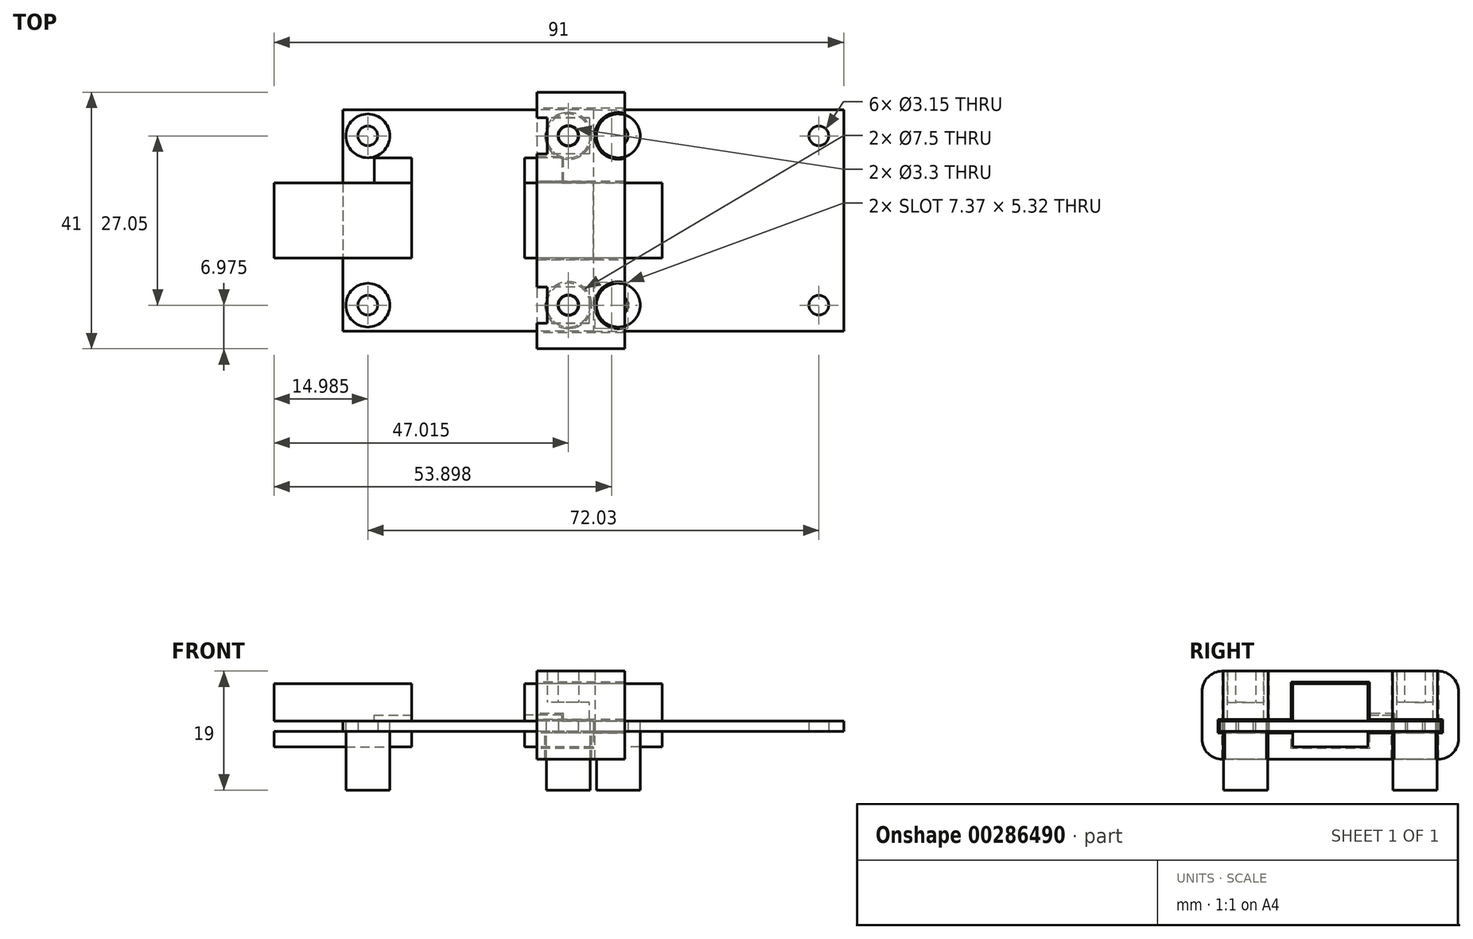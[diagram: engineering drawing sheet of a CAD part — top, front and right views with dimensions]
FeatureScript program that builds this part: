
annotation { "Feature Type Name" : "Feature", "Feature Type Description" : "" }
export const myFeature = defineFeature(function(context is Context, id is Id, definition is map)
    precondition{}
    {
        {
            var Q0;
            Q0=qCreatedBy(makeId("Top.planeOp"),FACE);
            var sketch = newSketch(context, id + "F0", { "sketchPlane" : qUnion([Q0])});
            skLineSegment(sketch, "E0.bottom", {"start": v(20, 17.7) * mm, "end": v(-20, 17.7) * mm});
            skLineSegment(sketch, "E0.top", {"start": v(20, -17.7) * mm, "end": v(-20, -17.7) * mm});
            skLineSegment(sketch, "E0.left", {"start": v(20, 17.7) * mm, "end": v(20, -17.7) * mm});
            skLineSegment(sketch, "E0.right", {"start": v(-20, 17.7) * mm, "end": v(-20, -17.7) * mm});
            skPoint(sketch, "E0.middle", {"position": v(0, 0) * mm});
            skCircle(sketch, "E1", {"center": v(-16.02, 13.52) * mm, "radius": 1.57 * mm});
            skCircle(sketch, "E2.MirrorC", {"center": v(16.02, 13.52) * mm, "radius": 1.57 * mm});
            skCircle(sketch, "E3.MirrorC", {"center": v(-16.02, -13.52) * mm, "radius": 1.57 * mm});
            skCircle(sketch, "E4.MirrorC", {"center": v(16.02, -13.52) * mm, "radius": 1.57 * mm});
            skSolve(sketch);
        }
        {
            var Q0;
            Q0 = qSketchRegion(id + "F0", true);
            extrude(context, id + "F1", {"entities" : qUnion([Q0]), "depth" : 1.6 * mm, "offsetDistance" : 25 * mm, "symmetric" : true});
        }
        {
            var Q0;
            Q0=makeQuery(id+"F1.opExtrude","CAP_FACE",FACE,{"disambiguationData":[OSD([sQuery(id+"F0.wireOp",EDGE,"E0.bottom"),sQuery(id+"F0.wireOp",EDGE,"E0.top"),sQuery(id+"F0.wireOp",EDGE,"E0.left"),sQuery(id+"F0.wireOp",EDGE,"E0.right"),sQuery(id+"F0.wireOp",EDGE,"E1"),sQuery(id+"F0.wireOp",EDGE,"E2.MirrorC"),sQuery(id+"F0.wireOp",EDGE,"E3.MirrorC"),sQuery(id+"F0.wireOp",EDGE,"E4.MirrorC")])],"isStart":false});
            var sketch = newSketch(context, id + "F2", { "sketchPlane" : qUnion([Q0])});
            skCircle(sketch, "E5", {"center": v(-16.02, 13.52) * mm, "radius": 3.5 * mm});
            skCircle(sketch, "E6", {"center": v(16.02, 13.52) * mm, "radius": 3.5 * mm});
            skCircle(sketch, "E7", {"center": v(16.02, -13.52) * mm, "radius": 3.5 * mm});
            skCircle(sketch, "E8", {"center": v(-16.02, -13.52) * mm, "radius": 3.5 * mm});
            skSolve(sketch);
        }
        {
            var Q0;
            Q0 = qSketchRegion(id + "F2", true);
            extrude(context, id + "F3", {"entities" : qUnion([Q0]), "oppositeDirection" : true, "depth" : 11 * mm, "offsetDistance" : 25 * mm});
        }
        {
            var Q0;
            Q0=makeQuery(id+"F1.opExtrude","SWEPT_FACE",FACE,{"disambiguationData":[OSD([sQuery(id+"F0.wireOp",EDGE,"E0.left")])]});
            var sketch = newSketch(context, id + "F4", { "sketchPlane" : qUnion([Q0])});
            skLineSegment(sketch, "E9.top", {"start": v(-6, -0.8) * mm, "end": v(6, -0.8) * mm});
            skLineSegment(sketch, "E10.MirrorCS", {"start": v(-6, 0.8) * mm, "end": v(6, 0.8) * mm});
            skLineSegment(sketch, "E11.bottom", {"start": v(6, 0.8) * mm, "end": v(10, 0.8) * mm});
            skLineSegment(sketch, "E11.top", {"start": v(6, 1.8) * mm, "end": v(10, 1.8) * mm});
            skLineSegment(sketch, "E11.left", {"start": v(6, 0.8) * mm, "end": v(6, 1.8) * mm});
            skLineSegment(sketch, "E11.right", {"start": v(10, 0.8) * mm, "end": v(10, 1.8) * mm});
            skLineSegment(sketch, "E12", {"start": v(-6, 0.8) * mm, "end": v(-6, 6.8) * mm});
            skLineSegment(sketch, "E13", {"start": v(-6, 6.8) * mm, "end": v(6, 6.8) * mm});
            skLineSegment(sketch, "E14", {"start": v(6, 6.8) * mm, "end": v(6, 0.8) * mm});
            skLineSegment(sketch, "E15", {"start": v(-6, -0.8) * mm, "end": v(-6, -3.3) * mm});
            skLineSegment(sketch, "E16", {"start": v(-6, -3.3) * mm, "end": v(6, -3.3) * mm});
            skLineSegment(sketch, "E17", {"start": v(6, -3.3) * mm, "end": v(6, -0.8) * mm});
            skSolve(sketch);
        }
        {
            var Q0;
            Q0 = qSketchRegion(id + "F4", true);
            extrude(context, id + "F5", {"entities" : qUnion([Q0]), "depth" : 22 * mm, "offsetDistance" : 25 * mm, "symmetric" : true});
        }
        {
            var Q0;
            Q0=makeQuery(id+"F5.opExtrude","CAP_FACE",FACE,{"disambiguationData":[OSD([sQuery(id+"F4.wireOp",EDGE,"E10.MirrorCS"),sQuery(id+"F4.wireOp",EDGE,"E11.bottom"),sQuery(id+"F4.wireOp",EDGE,"E11.top"),sQuery(id+"F4.wireOp",EDGE,"E11.right"),sQuery(id+"F4.wireOp",EDGE,"E12"),sQuery(id+"F4.wireOp",EDGE,"E13"),sQuery(id+"F4.wireOp",EDGE,"E14")])],"isStart":false});
            var sketch = newSketch(context, id + "F6", { "sketchPlane" : qUnion([Q0])});
            skLineSegment(sketch, "E18.bottom", {"start": v(6, 1.8) * mm, "end": v(10, 1.8) * mm});
            skLineSegment(sketch, "E18.top", {"start": v(6, 0.8) * mm, "end": v(10, 0.8) * mm});
            skLineSegment(sketch, "E18.left", {"start": v(6, 1.8) * mm, "end": v(6, 0.8) * mm});
            skLineSegment(sketch, "E18.right", {"start": v(10, 1.8) * mm, "end": v(10, 0.8) * mm});
            skSolve(sketch);
        }
        {
            var Q0;
            Q0 = qSketchRegion(id + "F6", true);
            extrude(context, id + "F7", {"entities" : qUnion([Q0]), "operationType" : NewBodyOperationType.REMOVE, "oppositeDirection" : true, "depth" : 16 * mm, "offsetDistance" : 25 * mm});
        }
        {
            var Q0;
            Q0=makeQuery(id+"F5.opExtrude","SWEPT_BODY",BODY,{"disambiguationData":[OSD([sQuery(id+"F4.wireOp",EDGE,"E9.bottom"),sQuery(id+"F4.wireOp",EDGE,"E9.top"),sQuery(id+"F4.wireOp",EDGE,"E9.left"),sQuery(id+"F4.wireOp",EDGE,"E9.right")])]});
            var Q1;
            Q1=makeQuery(id+"F5.opExtrude","SWEPT_BODY",BODY,{"disambiguationData":[OSD([sQuery(id+"F4.wireOp",EDGE,"d8b67e58-9760-4f35-8aba-aea9f4cf0cb30.MirrorCS"),sQuery(id+"F4.wireOp",EDGE,"fc04d03d-4783-4ae8-9673-6a9668c51ce80.MirrorCS"),sQuery(id+"F4.wireOp",EDGE,"E10.MirrorCS"),sQuery(id+"F4.wireOp",EDGE,"51854301-50fa-4171-bd93-f3eeceddffb40.MirrorCS")])]});
            var Q2;
            Q2=qCreatedBy(makeId("Right.planeOp"),FACE);
            mirror(context, id + "F8", {"entities" : qUnion([Q0, Q1]), "mirrorPlane" : qUnion([Q2])});
        }
        {
            var Q0;
            Q0=makeQuery(id+"F1.opExtrude","SWEPT_BODY",BODY,{"disambiguationData":[OSD([sQuery(id+"F0.wireOp",EDGE,"E0.bottom"),sQuery(id+"F0.wireOp",EDGE,"E0.top"),sQuery(id+"F0.wireOp",EDGE,"E0.left"),sQuery(id+"F0.wireOp",EDGE,"E0.right"),sQuery(id+"F0.wireOp",EDGE,"E1"),sQuery(id+"F0.wireOp",EDGE,"E2.MirrorC"),sQuery(id+"F0.wireOp",EDGE,"E3.MirrorC"),sQuery(id+"F0.wireOp",EDGE,"E4.MirrorC")])]});
            var Q1;
            Q1=makeQuery(id+"F3.opExtrude","SWEPT_BODY",BODY,{"disambiguationData":[OSD([sQuery(id+"F2.wireOp",EDGE,"E7")])]});
            var Q2;
            Q2=makeQuery(id+"F3.opExtrude","SWEPT_BODY",BODY,{"disambiguationData":[OSD([sQuery(id+"F2.wireOp",EDGE,"E6")])]});
            var Q3;
            Q3=makeQuery(id+"F1.opExtrude","SWEPT_FACE",FACE,{"disambiguationData":[OSD([sQuery(id+"F0.wireOp",EDGE,"E0.left")])]});
            mirror(context, id + "F9", {"entities" : qUnion([Q0, Q1, Q2]), "mirrorPlane" : qUnion([Q3])});
        }
        {
            var Q0;
            Q0=makeQuery(id+"F1.opExtrude","SWEPT_FACE",FACE,{"disambiguationData":[OSD([sQuery(id+"F0.wireOp",EDGE,"E0.left")])]});
            var sketch = newSketch(context, id + "F10", { "sketchPlane" : qUnion([Q0])});
            skLineSegment(sketch, "E19.bottom", {"start": v(-20.5, -5.3) * mm, "end": v(20.5, -5.3) * mm});
            skLineSegment(sketch, "E19.top", {"start": v(-20.5, 8.8) * mm, "end": v(20.5, 8.8) * mm});
            skLineSegment(sketch, "E19.left", {"start": v(-20.5, -5.3) * mm, "end": v(-20.5, 8.8) * mm});
            skLineSegment(sketch, "E19.right", {"start": v(20.5, -5.3) * mm, "end": v(20.5, 8.8) * mm});
            skPoint(sketch, "E19.middle", {"position": v(0, 1.75) * mm});
            skSolve(sketch);
        }
        {
            var Q0;
            Q0 = qSketchRegion(id + "F10", true);
            extrude(context, id + "F11", {"entities" : qUnion([Q0]), "oppositeDirection" : true, "depth" : 9 * mm, "offsetDistance" : 25 * mm, "hasSecondDirection" : true, "secondDirectionOppositeDirection" : false, "secondDirectionDepth" : 5 * mm});
        }
        {
            var Q0;
            Q0=makeQuery(id+"F3.opExtrude","SWEPT_BODY",BODY,{"disambiguationData":[OSD([sQuery(id+"F2.wireOp",EDGE,"E7")])]});
            var Q1;
            Q1=makeQuery(id+"F5.opExtrude","SWEPT_BODY",BODY,{"disambiguationData":[OSD([sQuery(id+"F4.wireOp",EDGE,"d8b67e58-9760-4f35-8aba-aea9f4cf0cb30.MirrorCS"),sQuery(id+"F4.wireOp",EDGE,"fc04d03d-4783-4ae8-9673-6a9668c51ce80.MirrorCS"),sQuery(id+"F4.wireOp",EDGE,"E10.MirrorCS"),sQuery(id+"F4.wireOp",EDGE,"51854301-50fa-4171-bd93-f3eeceddffb40.MirrorCS"),sQuery(id+"F4.wireOp",EDGE,"E11.bottom"),sQuery(id+"F4.wireOp",EDGE,"E11.top"),sQuery(id+"F4.wireOp",EDGE,"E11.right")])]});
            var Q2;
            Q2=makeQuery(id+"F9.opPattern","COPY",BODY,{"derivedFrom":makeQuery(id+"F3.opExtrude","SWEPT_BODY",BODY,{"disambiguationData":[OSD([sQuery(id+"F2.wireOp",EDGE,"E6")])]}),"instanceName":"1"});
            var Q3;
            Q3=makeQuery(id+"F3.opExtrude","SWEPT_BODY",BODY,{"disambiguationData":[OSD([sQuery(id+"F2.wireOp",EDGE,"E6")])]});
            var Q4;
            Q4=makeQuery(id+"F9.opPattern","COPY",BODY,{"derivedFrom":makeQuery(id+"F1.opExtrude","SWEPT_BODY",BODY,{"disambiguationData":[OSD([sQuery(id+"F0.wireOp",EDGE,"E0.bottom"),sQuery(id+"F0.wireOp",EDGE,"E0.top"),sQuery(id+"F0.wireOp",EDGE,"E0.left"),sQuery(id+"F0.wireOp",EDGE,"E0.right"),sQuery(id+"F0.wireOp",EDGE,"E1"),sQuery(id+"F0.wireOp",EDGE,"E2.MirrorC"),sQuery(id+"F0.wireOp",EDGE,"E3.MirrorC"),sQuery(id+"F0.wireOp",EDGE,"E4.MirrorC")])]}),"instanceName":"1"});
            var Q5;
            Q5=makeQuery(id+"F1.opExtrude","SWEPT_BODY",BODY,{"disambiguationData":[OSD([sQuery(id+"F0.wireOp",EDGE,"E0.bottom"),sQuery(id+"F0.wireOp",EDGE,"E0.top"),sQuery(id+"F0.wireOp",EDGE,"E0.left"),sQuery(id+"F0.wireOp",EDGE,"E0.right"),sQuery(id+"F0.wireOp",EDGE,"E1"),sQuery(id+"F0.wireOp",EDGE,"E2.MirrorC"),sQuery(id+"F0.wireOp",EDGE,"E3.MirrorC"),sQuery(id+"F0.wireOp",EDGE,"E4.MirrorC")])]});
            var Q6;
            Q6=makeQuery(id+"F9.opPattern","COPY",BODY,{"derivedFrom":makeQuery(id+"F3.opExtrude","SWEPT_BODY",BODY,{"disambiguationData":[OSD([sQuery(id+"F2.wireOp",EDGE,"E7")])]}),"instanceName":"1"});
            var Q7;
            Q7=makeQuery(id+"F8.opPattern","COPY",BODY,{"derivedFrom":makeQuery(id+"F5.opExtrude","SWEPT_BODY",BODY,{"disambiguationData":[OSD([sQuery(id+"F4.wireOp",EDGE,"d8b67e58-9760-4f35-8aba-aea9f4cf0cb30.MirrorCS"),sQuery(id+"F4.wireOp",EDGE,"fc04d03d-4783-4ae8-9673-6a9668c51ce80.MirrorCS"),sQuery(id+"F4.wireOp",EDGE,"E10.MirrorCS"),sQuery(id+"F4.wireOp",EDGE,"51854301-50fa-4171-bd93-f3eeceddffb40.MirrorCS"),sQuery(id+"F4.wireOp",EDGE,"E11.bottom"),sQuery(id+"F4.wireOp",EDGE,"E11.top"),sQuery(id+"F4.wireOp",EDGE,"E11.right")])]}),"instanceName":"1"});
            var Q8;
            Q8=makeQuery(id+"F8.opPattern","COPY",BODY,{"derivedFrom":makeQuery(id+"F5.opExtrude","SWEPT_BODY",BODY,{"disambiguationData":[OSD([sQuery(id+"F4.wireOp",EDGE,"E9.bottom"),sQuery(id+"F4.wireOp",EDGE,"E9.top"),sQuery(id+"F4.wireOp",EDGE,"E9.left"),sQuery(id+"F4.wireOp",EDGE,"E9.right")])]}),"instanceName":"1"});
            var Q9;
            Q9=makeQuery(id+"F5.opExtrude","SWEPT_BODY",BODY,{"disambiguationData":[OSD([sQuery(id+"F4.wireOp",EDGE,"E9.bottom"),sQuery(id+"F4.wireOp",EDGE,"E9.top"),sQuery(id+"F4.wireOp",EDGE,"E9.left"),sQuery(id+"F4.wireOp",EDGE,"E9.right")])]});
            var Q10;
            Q10=makeQuery(id+"F3.opExtrude","SWEPT_BODY",BODY,{"disambiguationData":[OSD([sQuery(id+"F2.wireOp",EDGE,"E8")])]});
            var Q11;
            Q11=makeQuery(id+"F3.opExtrude","SWEPT_BODY",BODY,{"disambiguationData":[OSD([sQuery(id+"F2.wireOp",EDGE,"E5")])]});
            var Q12;
            Q12=makeQuery(id+"F11.opExtrude","SWEPT_BODY",BODY,{"disambiguationData":[OSD([sQuery(id+"F10.wireOp",EDGE,"E19.bottom"),sQuery(id+"F10.wireOp",EDGE,"E19.top"),sQuery(id+"F10.wireOp",EDGE,"E19.left"),sQuery(id+"F10.wireOp",EDGE,"E19.right")])]});
            booleanBodies(context, id + "F12", {"operationType" : BooleanOperationType.SUBTRACTION, "tools" : qUnion([Q0, Q1, Q2, Q3, Q4, Q5, Q6, Q7, Q8, Q9, Q10, Q11]), "targets" : qUnion([Q12]), "offset" : true, "offsetAll" : true, "offsetDistance" : .25 * mm, "keepTools" : true});
        }
        {
            var Q0;
            Q0=makeQuery(id+"F11.opExtrude","SWEPT_FACE",FACE,{"disambiguationData":[OSD([sQuery(id+"F10.wireOp",EDGE,"E19.bottom")])]});
            var sketch = newSketch(context, id + "F13", { "sketchPlane" : qUnion([Q0])});
            skArc(sketch, "E20.0", {"start": v(25, -9.91) * mm, "mid": v(20.24, -13.52) * mm, "end": v(25, -17.14) * mm});
            skArc(sketch, "E21.0", {"start": v(25, 17.14) * mm, "mid": v(20.23, 13.53) * mm, "end": v(25, 9.91) * mm});
            skLineSegment(sketch, "E22", {"start": v(25, -17.14) * mm, "end": v(25, -9.91) * mm});
            skLineSegment(sketch, "E23", {"start": v(25, 9.91) * mm, "end": v(25, 17.14) * mm});
            skSolve(sketch);
        }
        {
            var Q0;
            Q0 = qSketchRegion(id + "F13", true);
            extrude(context, id + "F14", {"entities" : qUnion([Q0]), "operationType" : NewBodyOperationType.REMOVE, "oppositeDirection" : true, "depth" : 25 * mm, "offsetDistance" : 25 * mm});
        }
        {
            var Q0;
            Q0=makeQuery(id+"F17.opFillet","SPLIT",FACE,{"disambiguationData":[OD(2.0)],"derivedFrom":makeQuery(id+"F11.opExtrude","SWEPT_FACE",FACE,{"disambiguationData":[OSD([sQuery(id+"F10.wireOp",EDGE,"E19.top")])]})});
            var sketch = newSketch(context, id + "F15", { "sketchPlane" : qUnion([Q0])});
            skCircle(sketch, "E24.cCircle", {"center": v(16.02, -13.52) * mm, "radius": 2.75 * mm, "construction": true});
            skLineSegment(sketch, "E24.0", {"start": v(14.43, -10.77) * mm, "end": v(17.6, -10.77) * mm, "construction": true});
            skLineSegment(sketch, "E24.1", {"start": v(17.6, -10.77) * mm, "end": v(19.2, -13.52) * mm, "construction": true});
            skLineSegment(sketch, "E24.2", {"start": v(19.2, -13.52) * mm, "end": v(17.6, -16.27) * mm, "construction": true});
            skLineSegment(sketch, "E24.3", {"start": v(17.6, -16.27) * mm, "end": v(14.43, -16.27) * mm, "construction": true});
            skLineSegment(sketch, "E24.4", {"start": v(14.43, -16.28) * mm, "end": v(12.84, -13.52) * mm, "construction": true});
            skLineSegment(sketch, "E24.5", {"start": v(12.84, -13.52) * mm, "end": v(14.43, -10.77) * mm, "construction": true});
            skPoint(sketch, "E24.0.midPoint", {"position": v(16.02, -10.77) * mm});
            skLineSegment(sketch, "E25", {"start": v(11, -10.62) * mm, "end": v(19.4, -10.62) * mm});
            skLineSegment(sketch, "E26", {"start": v(19.4, -10.62) * mm, "end": v(19.4, -16.42) * mm});
            skLineSegment(sketch, "E27", {"start": v(19.4, -16.42) * mm, "end": v(11, -16.42) * mm});
            skLineSegment(sketch, "E28.MirrorCS", {"start": v(11, 10.62) * mm, "end": v(19.4, 10.62) * mm});
            skLineSegment(sketch, "E29.MirrorCS", {"start": v(19.4, 10.62) * mm, "end": v(19.4, 16.42) * mm});
            skLineSegment(sketch, "E30.MirrorCS", {"start": v(19.4, 16.42) * mm, "end": v(11, 16.42) * mm});
            skLineSegment(sketch, "E31", {"start": v(11, 16.42) * mm, "end": v(11, 10.62) * mm});
            skLineSegment(sketch, "E32", {"start": v(11, -10.62) * mm, "end": v(11, -16.42) * mm});
            skSolve(sketch);
        }
        {
            var Q0;
            {var subQ0=sQuery(id+"F15.wireOp",EDGE,"57f893ae-c056-44ca-b560-d6d7a5f4ef840.MirrorC");var subQ1=sQuery(id+"F15.wireOp",EDGE,"E28.MirrorCS");var subQ2=makeQuery(id+"F15.imprint","INTERSECT",VERTEX,{"disambiguationData":[OD(0.0)],"derivedFrom":[subQ1,subQ0]});Q0=makeQuery(id+"F15.imprint","IMPRINT",FACE,{"disambiguationData":[TD([[makeQuery(id+"F15.imprint","IMPRINT",EDGE,{"disambiguationData":[TD([[subQ2,-1.0]])],"derivedFrom":subQ1}),1.0]])]});}
            var Q1;
            {var subQ0=sQuery(id+"F15.wireOp",EDGE,"E31");Q1=makeQuery(id+"F15.imprint","IMPRINT",FACE,{"disambiguationData":[TD([[makeQuery(id+"F15.imprint","IMPRINT",EDGE,{"derivedFrom":subQ0}),-1.0]])]});}
            var Q2;
            Q2=makeQuery(id+"F15.imprint","IMPRINT",FACE,{"disambiguationData":[TD([[makeQuery(id+"F15.imprint","IMPRINT",EDGE,{"derivedFrom":sQuery(id+"F15.wireOp",EDGE,"E25")}),-1.0]])]});
            var Q3;
            {var subQ0=makeQuery(id+"F1.opExtrude","CAP_FACE",FACE,{"disambiguationData":[OSD([sQuery(id+"F0.wireOp",EDGE,"E0.bottom"),sQuery(id+"F0.wireOp",EDGE,"E0.top"),sQuery(id+"F0.wireOp",EDGE,"E0.left"),sQuery(id+"F0.wireOp",EDGE,"E0.right"),sQuery(id+"F0.wireOp",EDGE,"E1"),sQuery(id+"F0.wireOp",EDGE,"E2.MirrorC"),sQuery(id+"F0.wireOp",EDGE,"E3.MirrorC"),sQuery(id+"F0.wireOp",EDGE,"E4.MirrorC")])],"isStart":false});Q3=makeQuery(id+"FdNvlJCd8aFrhzl_8.boolean.opBoolean","MERGE",FACE,{"derivedFrom":[makeQuery(id+"F12.tempBoolean.opBoolean","MERGE",FACE,{"disambiguationData":[OD(1.0)],"derivedFrom":[],"fromTools":[makeQuery(id+"F12.offsetTempBody.opPattern","COPY",FACE,{"derivedFrom":subQ0,"instanceName":"1"}),makeQuery(id+"F12.offsetTempBody.opPattern","COPY",FACE,{"derivedFrom":makeQuery(id+"F9.opPattern","COPY",FACE,{"derivedFrom":subQ0,"instanceName":"1"}),"instanceName":"1"})]}),makeQuery(id+"FdNvlJCd8aFrhzl_8.opExtrude","CAP_FACE",FACE,{"disambiguationData":[OSD([sQuery(id+"F15.wireOp",EDGE,"E28.MirrorCS"),sQuery(id+"F15.wireOp",EDGE,"57f893ae-c056-44ca-b560-d6d7a5f4ef840.MirrorC"),sQuery(id+"F15.wireOp",EDGE,"E29.MirrorCS"),sQuery(id+"F15.wireOp",EDGE,"E30.MirrorCS"),sQuery(id+"F15.wireOp",EDGE,"E31")])],"isStart":false})]});}
            extrude(context, id + "F16", {"entities" : qUnion([Q0, Q1, Q2]), "operationType" : NewBodyOperationType.REMOVE, "endBound" : BoundingType.UP_TO_SURFACE, "oppositeDirection" : true, "depth" : 25 * mm, "endBoundEntityFace" : qUnion([Q3]), "offsetDistance" : 25 * mm});
        }
        {
            var Q0;
            Q0=makeQuery(id+"F11.opExtrude","SWEPT_EDGE",EDGE,{"disambiguationData":[OSD([sQuery(id+"F10.wireOp",EDGE,"E19.top"),sQuery(id+"F10.wireOp",EDGE,"E19.left")])]});
            var Q1;
            Q1=makeQuery(id+"F11.opExtrude","SWEPT_EDGE",EDGE,{"disambiguationData":[OSD([sQuery(id+"F10.wireOp",EDGE,"E19.top"),sQuery(id+"F10.wireOp",EDGE,"E19.right")])]});
            var Q2;
            Q2=makeQuery(id+"F11.opExtrude","SWEPT_EDGE",EDGE,{"disambiguationData":[OSD([sQuery(id+"F10.wireOp",EDGE,"E19.bottom"),sQuery(id+"F10.wireOp",EDGE,"E19.right")])]});
            var Q3;
            Q3=makeQuery(id+"F11.opExtrude","SWEPT_EDGE",EDGE,{"disambiguationData":[OSD([sQuery(id+"F10.wireOp",EDGE,"E19.bottom"),sQuery(id+"F10.wireOp",EDGE,"E19.left")])]});
            fillet(context, id + "F17", {"entities" : qUnion([Q0, Q1, Q2, Q3]), "tangentPropagation" : true, "radius" : 3.3 * mm, "defaultsChanged" : false, "vertexSettings" : [], "allowEdgeOverflow" : false});
        }
        {
            var Q0;
            Q0=makeQuery(id+"F1.opExtrude","CAP_FACE",FACE,{"disambiguationData":[OSD([sQuery(id+"F0.wireOp",EDGE,"E0.bottom"),sQuery(id+"F0.wireOp",EDGE,"E0.top"),sQuery(id+"F0.wireOp",EDGE,"E0.left"),sQuery(id+"F0.wireOp",EDGE,"E0.right"),sQuery(id+"F0.wireOp",EDGE,"E1"),sQuery(id+"F0.wireOp",EDGE,"E2.MirrorC"),sQuery(id+"F0.wireOp",EDGE,"E3.MirrorC"),sQuery(id+"F0.wireOp",EDGE,"E4.MirrorC")])],"isStart":false});
            var sketch = newSketch(context, id + "F18", { "sketchPlane" : qUnion([Q0])});
            skLineSegment(sketch, "E33.bottom", {"start": v(19.4, 16.42) * mm, "end": v(12.64, 16.42) * mm});
            skLineSegment(sketch, "E33.top", {"start": v(19.4, 10.62) * mm, "end": v(12.64, 10.62) * mm});
            skLineSegment(sketch, "E33.left", {"start": v(19.4, 16.42) * mm, "end": v(19.4, 10.62) * mm});
            skLineSegment(sketch, "E33.right", {"start": v(12.64, 16.42) * mm, "end": v(12.64, 10.62) * mm});
            skPoint(sketch, "E33.middle", {"position": v(16.02, 13.52) * mm});
            skCircle(sketch, "E34", {"center": v(16.02, 13.52) * mm, "radius": 1.65 * mm});
            skLineSegment(sketch, "E35.MirrorCS", {"start": v(19.4, -16.42) * mm, "end": v(19.4, -10.62) * mm});
            skPoint(sketch, "E36.MirrorP", {"position": v(16.02, -13.52) * mm});
            skLineSegment(sketch, "E37.MirrorCS", {"start": v(19.4, -16.42) * mm, "end": v(12.64, -16.42) * mm});
            skLineSegment(sketch, "E38.MirrorCS", {"start": v(19.4, -10.62) * mm, "end": v(12.64, -10.62) * mm});
            skLineSegment(sketch, "E39.MirrorCS", {"start": v(12.64, -16.42) * mm, "end": v(12.64, -10.62) * mm});
            skCircle(sketch, "E40.MirrorC", {"center": v(16.02, -13.52) * mm, "radius": 1.65 * mm});
            skSolve(sketch);
        }
        {
            var Q0;
            Q0 = qSketchRegion(id + "F18", true);
            var Q1;
            Q1=makeQuery(id+"F17.opFillet","SPLIT",FACE,{"disambiguationData":[OD(2.0)],"derivedFrom":makeQuery(id+"F11.opExtrude","SWEPT_FACE",FACE,{"disambiguationData":[OSD([sQuery(id+"F10.wireOp",EDGE,"E19.top")])]})});
            var Q2;
            Q2=makeQuery(id+"F17.opFillet","SPLIT",FACE,{"disambiguationData":[OD(2.0)],"derivedFrom":makeQuery(id+"F11.opExtrude","SWEPT_FACE",FACE,{"disambiguationData":[OSD([sQuery(id+"F10.wireOp",EDGE,"E19.top")])]})});
            extrude(context, id + "F19", {"entities" : qUnion([Q0]), "operationType" : NewBodyOperationType.ADD, "endBound" : BoundingType.UP_TO_SURFACE, "depth" : 3 * mm, "endBoundEntityFace" : qUnion([Q1]), "offsetDistance" : 25 * mm, "hasSecondDirection" : true, "secondDirectionOppositeDirection" : false, "secondDirectionDepth" : 3 * mm, "secondDirectionBoundEntityFace" : qUnion([Q2])});
        }
        {
            var Q0;
            {var subQ1=sQuery(id+"F10.wireOp",EDGE,"E19.bottom");Q0=makeQuery(id+"F12.tempBoolean.opBoolean","SPLIT",FACE,{"disambiguationData":[TD([makeQuery(id+"F12.offsetTempBody.opPattern","COPY",FACE,{"derivedFrom":makeQuery(id+"F5.opExtrude","SWEPT_FACE",FACE,{"disambiguationData":[OSD([sQuery(id+"F4.wireOp",EDGE,"E15")])]}),"instanceName":"1"})])],"derivedFrom":makeQuery(id+"F11.opExtrude","CAP_FACE",FACE,{"disambiguationData":[OSD([subQ1,sQuery(id+"F10.wireOp",EDGE,"E19.top"),sQuery(id+"F10.wireOp",EDGE,"E19.left"),sQuery(id+"F10.wireOp",EDGE,"E19.right")])],"isStart":true})});}
            var sketch = newSketch(context, id + "F20", { "sketchPlane" : qUnion([Q0])});
            skLineSegment(sketch, "E41.bottom", {"start": v(6.25, -3.55) * mm, "end": v(-6.25, -3.55) * mm});
            skLineSegment(sketch, "E41.top", {"start": v(6.25, -1.05) * mm, "end": v(-6.25, -1.05) * mm});
            skLineSegment(sketch, "E41.left", {"start": v(-6.25, -3.55) * mm, "end": v(-6.25, -1.05) * mm});
            skLineSegment(sketch, "E41.right", {"start": v(6.25, -3.55) * mm, "end": v(6.25, -1.05) * mm});
            skSolve(sketch);
        }
        {
            var Q0;
            Q0 = qSketchRegion(id + "F20", true);
            extrude(context, id + "F21", {"entities" : qUnion([Q0]), "operationType" : NewBodyOperationType.ADD, "oppositeDirection" : true, "depth" : 5 * mm, "offsetDistance" : 25 * mm});
        }
    });
